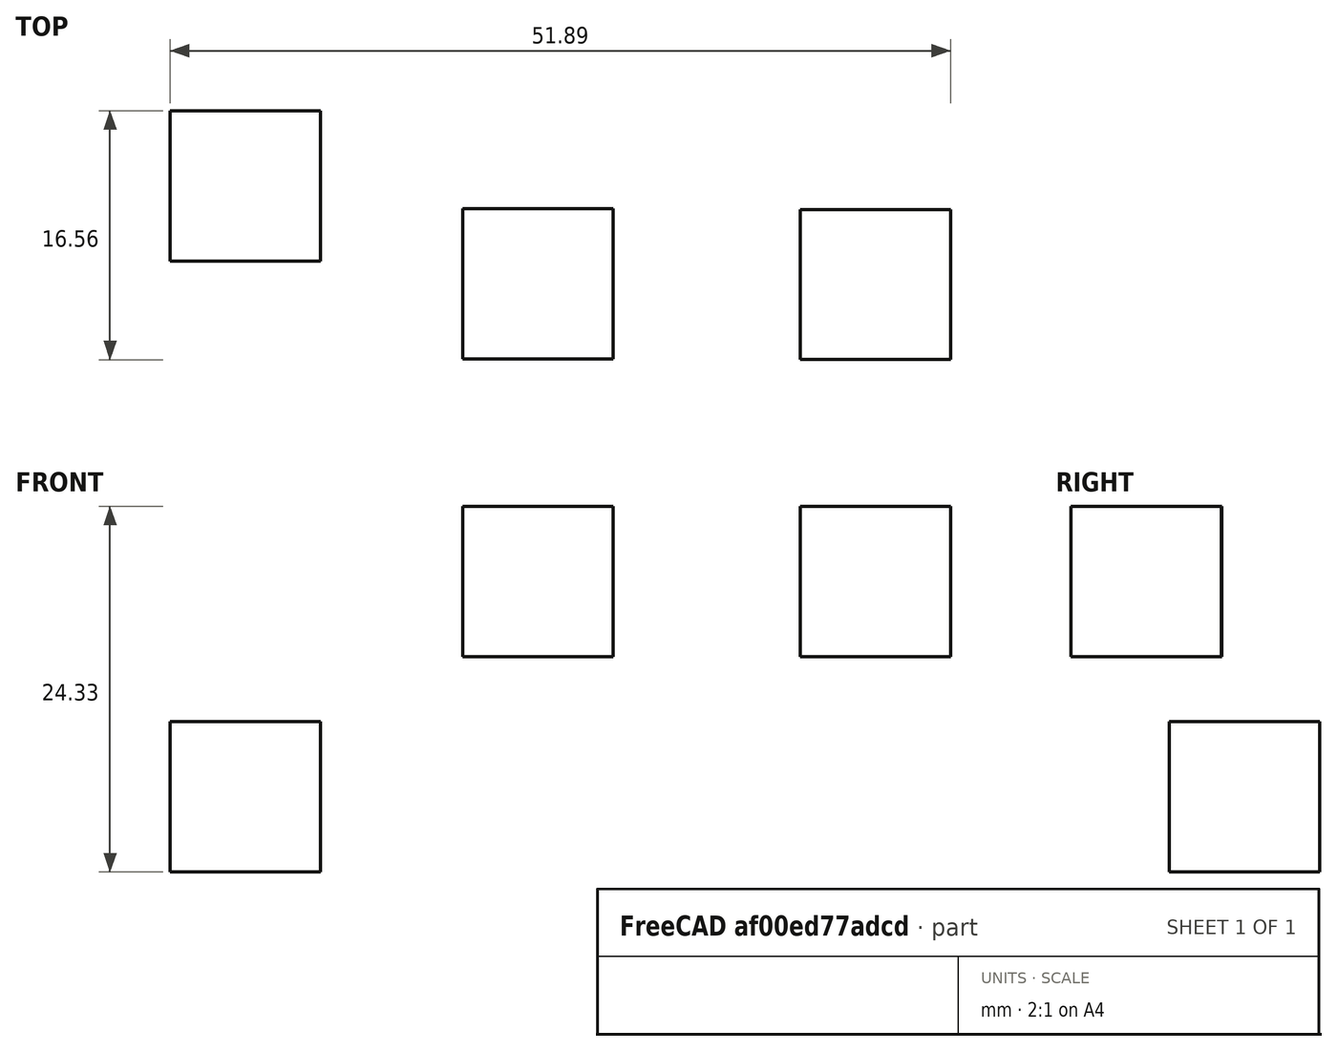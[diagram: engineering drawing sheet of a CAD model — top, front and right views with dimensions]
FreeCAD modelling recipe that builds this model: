
FCSTD DOCUMENT  (FreeCAD 0.15R4543 (Git))
Label: testAssembly10-block_iregular_constraint_order
License: All rights reserved
LicenseURL: http://en.wikipedia.org/wiki/All_rights_reserved
objects: Part::Box×3, App::FeaturePython×2
note: 3 computed .brp shape members not serialized (recipe doc carries the construction recipe); baked Part::Feature solids carry a one-line shape summary decoded from their .brp

FEATURE [Part::Box] Box  label="Cube"
  Height = 10
  Length = 10
  Placement = pos=(-19.4495,6.50937,-2.47472) rot=(0,0,1;0rad)
  Width = 10
FEATURE [Part::Box] Box001  label="Cube001"
  Height = 10
  Length = 10
  Placement = pos=(22.4429,-0.0453386,11.8595) rot=(0,0,1;0rad)
  Width = 10
FEATURE [Part::Box] Box002  label="Cube002"
  Height = 10
  Length = 10
  Placement = pos=(0,0,11.8595) rot=(0,0,1;0rad)
  Width = 10
FEATURE [App::FeaturePython] planeConstraint01  # a2plus constraint (typed FeaturePython)
  Object1 = Box002
  Object2 = Box001
  SubElement1 = Face6
  SubElement2 = Face6
  Type = plane
  directionConstraint = 0
  offset = 0
FEATURE [App::FeaturePython] planeConstraint02  # a2plus constraint (typed FeaturePython)
  Object1 = Box
  Object2 = Box001
  SubElement1 = Face6
  SubElement2 = Face6
  Type = plane
  directionConstraint = 0
  offset = 0
